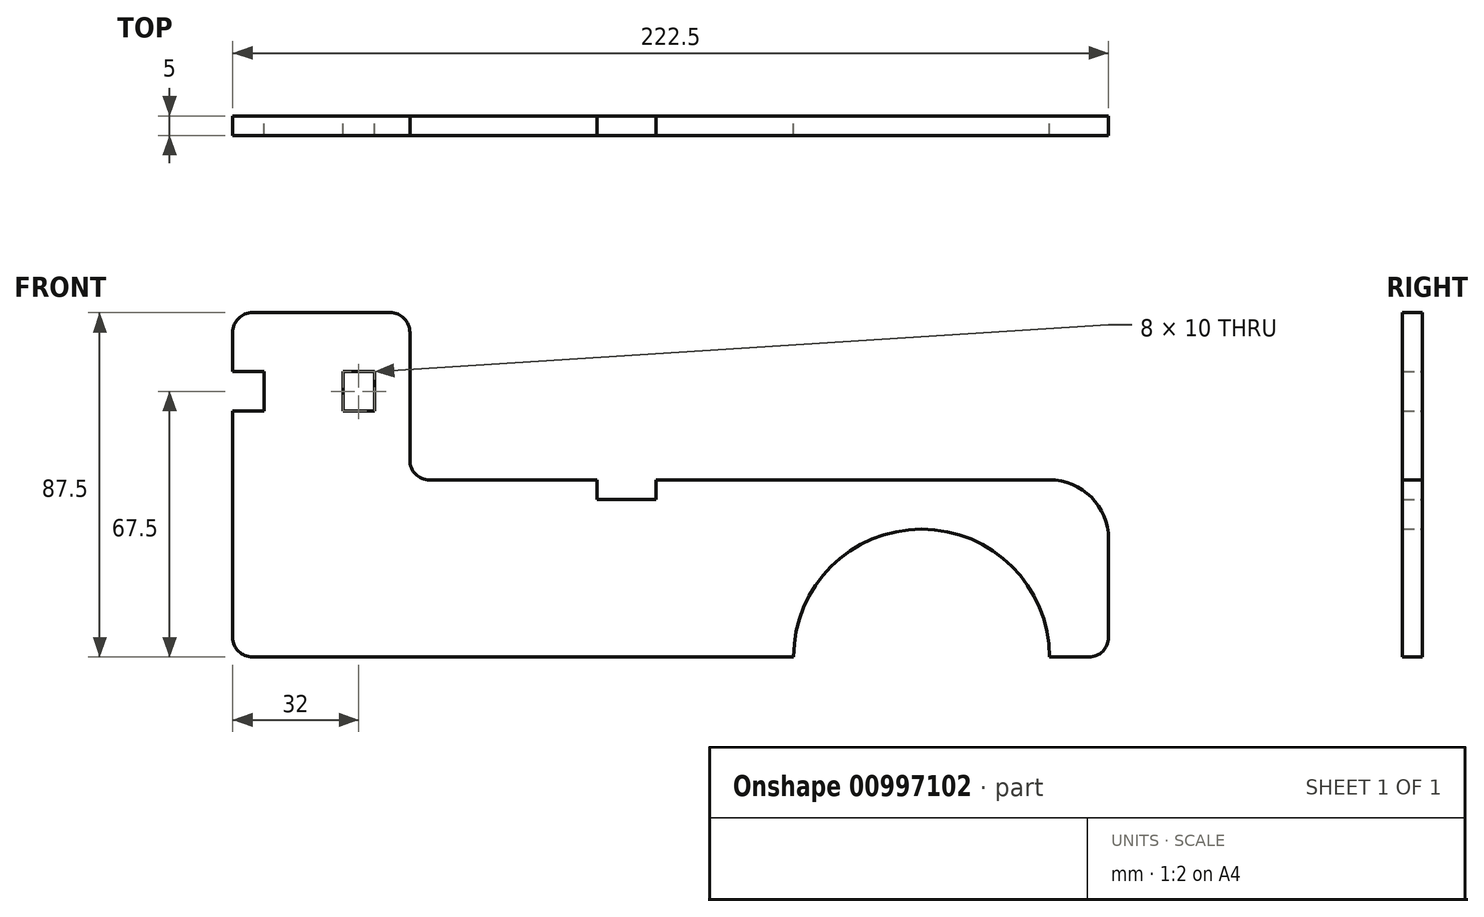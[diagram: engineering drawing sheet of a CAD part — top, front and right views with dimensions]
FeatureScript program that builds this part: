
annotation { "Feature Type Name" : "Feature", "Feature Type Description" : "" }
export const myFeature = defineFeature(function(context is Context, id is Id, definition is map)
    precondition{}
    {
        {
            var Q0;
            Q0=qCreatedBy(makeId("Front.planeOp"),FACE);
            var sketch = newSketch(context, id + "F0", { "sketchPlane" : qUnion([Q0])});
            skArc(sketch, "E0", {"start": v(32.5, 0) * mm, "mid": v(0, 32.5) * mm, "end": v(-32.5, 0) * mm});
            skLineSegment(sketch, "E1", {"start": v(-32.5, 0) * mm, "end": v(-170, 0) * mm});
            skLineSegment(sketch, "E2", {"start": v(-175, 5) * mm, "end": v(-175, 62.5) * mm});
            skLineSegment(sketch, "E3", {"start": v(-170, 87.5) * mm, "end": v(-135, 87.5) * mm});
            skLineSegment(sketch, "E4", {"start": v(-130, 82.5) * mm, "end": v(-130, 50) * mm});
            skLineSegment(sketch, "E5", {"start": v(-125, 45) * mm, "end": v(-82.5, 45) * mm});
            skLineSegment(sketch, "E6", {"start": v(47.5, 30) * mm, "end": v(47.5, 5) * mm});
            skLineSegment(sketch, "E7", {"start": v(42.5, 0) * mm, "end": v(32.5, 0) * mm});
            skPoint(sketch, "E8.visualSharp", {"position": v(47.5, 45) * mm});
            skArc(sketch, "E8.filletArc", {"start": v(47.5, 30) * mm, "mid": v(43.1, 40.6) * mm, "end": v(32.5, 45) * mm});
            skLineSegment(sketch, "E9", {"start": v(-82.5, 45) * mm, "end": v(-82.5, 40) * mm});
            skLineSegment(sketch, "E10", {"start": v(-82.5, 40) * mm, "end": v(-67.5, 40) * mm});
            skLineSegment(sketch, "E11", {"start": v(-67.5, 40) * mm, "end": v(-67.5, 45) * mm});
            skLineSegment(sketch, "E12.trimOffspring", {"start": v(-67.5, 45) * mm, "end": v(32.5, 45) * mm});
            skPoint(sketch, "E13", {"position": v(-75, 40) * mm});
            skPoint(sketch, "E14.visualSharp", {"position": v(-130, 45) * mm});
            skArc(sketch, "E14.filletArc", {"start": v(-130, 50) * mm, "mid": v(-128.54, 46.46) * mm, "end": v(-125, 45) * mm});
            skPoint(sketch, "E15.visualSharp", {"position": v(-175, 0) * mm});
            skArc(sketch, "E15.filletArc", {"start": v(-175, 5) * mm, "mid": v(-173.54, 1.46) * mm, "end": v(-170, 0) * mm});
            skLineSegment(sketch, "E16", {"start": v(-175, 72.5) * mm, "end": v(-167, 72.5) * mm});
            skLineSegment(sketch, "E17", {"start": v(-167, 72.5) * mm, "end": v(-167, 62.5) * mm});
            skLineSegment(sketch, "E18", {"start": v(-167, 62.5) * mm, "end": v(-175, 62.5) * mm});
            skLineSegment(sketch, "E19.trimOffspring", {"start": v(-175, 72.5) * mm, "end": v(-175, 82.5) * mm});
            skLineSegment(sketch, "E20.bottom", {"start": v(-147, 72.5) * mm, "end": v(-139, 72.5) * mm});
            skLineSegment(sketch, "E20.top", {"start": v(-147, 62.5) * mm, "end": v(-139, 62.5) * mm});
            skLineSegment(sketch, "E20.left", {"start": v(-147, 72.5) * mm, "end": v(-147, 62.5) * mm});
            skLineSegment(sketch, "E20.right", {"start": v(-139, 72.5) * mm, "end": v(-139, 62.5) * mm});
            skPoint(sketch, "E21.visualSharp", {"position": v(-175, 87.5) * mm});
            skArc(sketch, "E21.filletArc", {"start": v(-170, 87.5) * mm, "mid": v(-173.54, 86.04) * mm, "end": v(-175, 82.5) * mm});
            skPoint(sketch, "E22.visualSharp", {"position": v(-130, 87.5) * mm});
            skArc(sketch, "E22.filletArc", {"start": v(-130, 82.5) * mm, "mid": v(-131.46, 86.04) * mm, "end": v(-135, 87.5) * mm});
            skPoint(sketch, "E23.visualSharp", {"position": v(47.5, 0) * mm});
            skArc(sketch, "E23.filletArc", {"start": v(42.5, 0) * mm, "mid": v(46.04, 1.46) * mm, "end": v(47.5, 5) * mm});
            skSolve(sketch);
        }
        {
            var Q0;
            Q0 = qSketchRegion(id + "F0", true);
            extrude(context, id + "F1", {"entities" : qUnion([Q0]), "depth" : 5 * mm, "offsetDistance" : 25 * mm});
        }
    });
